# Revit family: 318_3f2bfc0881b34b889f015fee260085
name_source: partatom
category: Pipe Accessories
units: mm (PartAtom-declared; Revit-internal decimal feet)

## family parameters
Always vertical = Yes
Cut with Voids When Loaded = No
Part Type = Valve - Normal
Round Connector Dimension = Use Diameter
Shared = No
Work Plane-Based = No

## types (1)
- Manifold SL 1” - 3 Circuits
    BO1 = 77 mm
    BV1 = No
    CXIO1 = 17 mm  [stored 0.0557743 ft]
    CXO1 = 50 mm  [stored 0.164042 ft]
    DBB2 = 100 mm  [stored 0.328084 ft]
    Description = Manifold SL 1” - 3 Circuits - Material: PA6.6+Glass fiber
    L_2 = 127 mm
    MC Product Code = Manifold SL 1” - 3 Circuits
    MP1 = 32 mm
    MP3 = 32 mm
    Manufacturer = Eurotherm
    QmdConnectorList = 321;MP1;322;SPD1;323;SPD2;324;SPD3;351;MP3;352;RPD1;353;RPD2;354;RPD3
    RPD1 = 20 mm
    RPD2 = 20 mm
    RPD3 = 20 mm
    RYO1 = 52 mm
    RZO1 = 63 mm  [stored 0.206693 ft]
    SCO1 = 2 mm  [stored 0.00656168 ft]
    SMH1_ = 27 mm  [stored 0.0885827 ft]
    SML1 = 150 mm  [stored 0.492126 ft]
    SMR1 = 23 mm  [stored 0.0754593 ft]
    SMW1 = 50 mm  [stored 0.164042 ft]
    SMW1_ = 25 mm  [stored 0.082021 ft]
    SMW1__ve = -50 mm  [stored -0.164042 ft]
    SPD1 = 20 mm
    SPD2 = 20 mm
    SPD3 = 20 mm
    STL1 = 59 mm
    SYO1 = 36 mm  [stored 0.11811 ft]
    SZO1 = 273 mm
    TH_2 = 177 mm
    URL = https://www.eurotherm.info
    magiPartTypeId = 318
    magiProductFamilyId = 3f2bfc0881b34b889f015fee260085
    magiProductId = 3f2bfc0881b34b889f015fee260085

note: [stored X ft] marks values corroborated as IEEE doubles in the binary element streams (Revit-internal decimal feet)

## geometry (parser evidence)
native form markers: Sweep x3
no freeform markers — native parametric forms only
